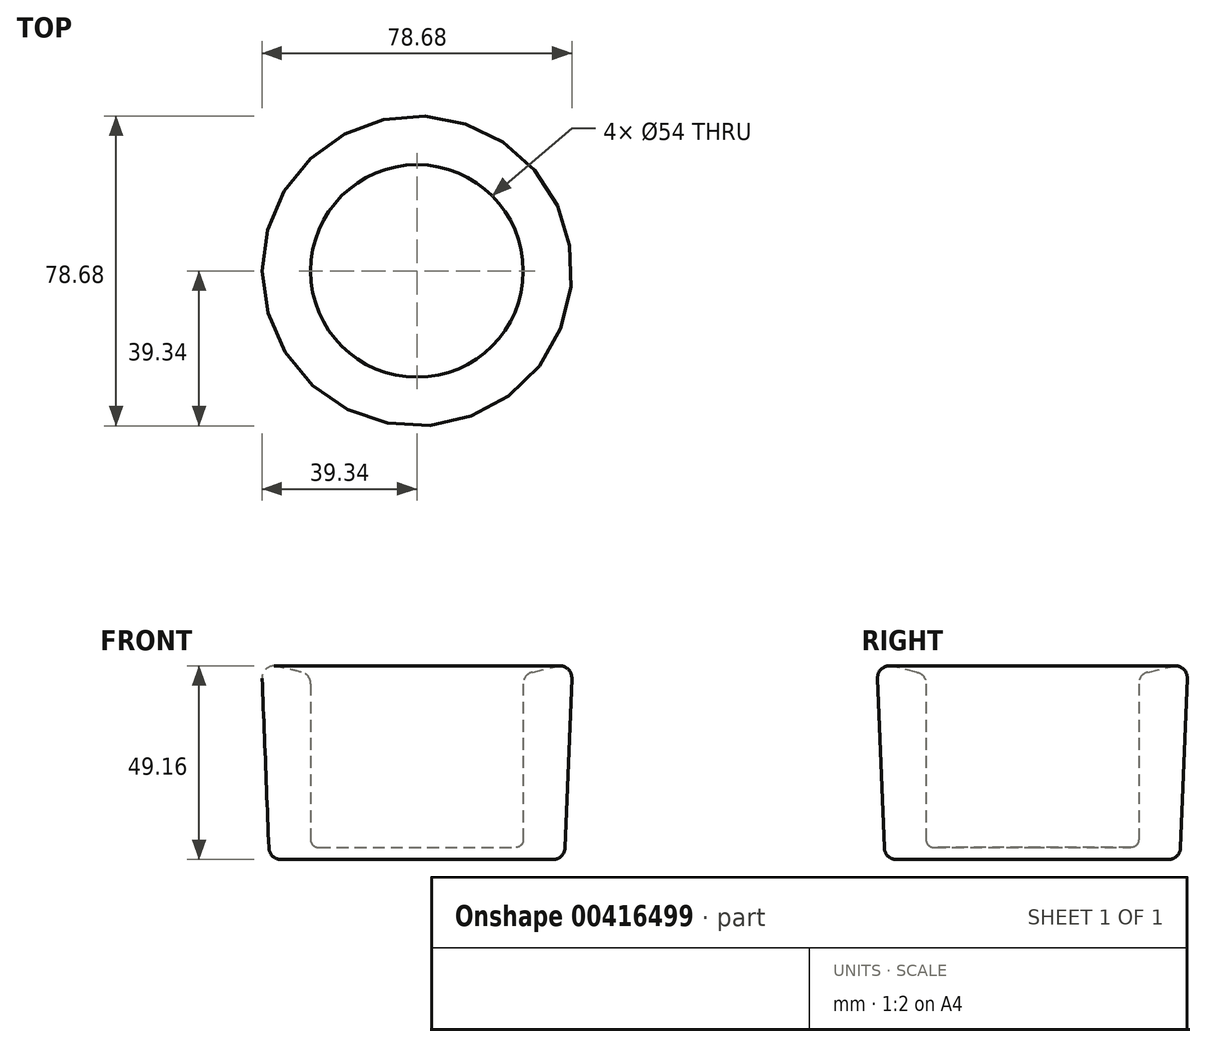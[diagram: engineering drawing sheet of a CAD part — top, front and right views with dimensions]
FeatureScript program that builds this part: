
annotation { "Feature Type Name" : "Feature", "Feature Type Description" : "" }
export const myFeature = defineFeature(function(context is Context, id is Id, definition is map)
    precondition{}
    {
        {
            var Q0;
            Q0=qCreatedBy(makeId("Right.planeOp"),FACE);
            var sketch = newSketch(context, id + "F0", { "sketchPlane" : qUnion([Q0])});
            skLineSegment(sketch, "E0", {"start": v(-39.34, 46.04) * mm, "end": v(-37.62, 2.88) * mm});
            skLineSegment(sketch, "E1", {"start": v(0, 3) * mm, "end": v(-25, 3) * mm});
            skLineSegment(sketch, "E2", {"start": v(-27, 5) * mm, "end": v(-27, 44.63) * mm});
            skLineSegment(sketch, "E3", {"start": v(-29.3, 47.55) * mm, "end": v(-35.64, 49.07) * mm});
            skLineSegment(sketch, "E4", {"start": v(-34.62, 0) * mm, "end": v(0, 0) * mm});
            skLineSegment(sketch, "E5", {"start": v(0, 0) * mm, "end": v(0, 3) * mm});
            skPoint(sketch, "E6.visualSharp", {"position": v(-39.5, 50) * mm});
            skArc(sketch, "E6.filletArc", {"start": v(-35.64, 49.07) * mm, "mid": v(-38.25, 48.48) * mm, "end": v(-39.34, 46.04) * mm});
            skPoint(sketch, "E7.visualSharp", {"position": v(-27, 47) * mm});
            skArc(sketch, "E7.filletArc", {"start": v(-27, 44.63) * mm, "mid": v(-27.64, 46.5) * mm, "end": v(-29.3, 47.55) * mm});
            skPoint(sketch, "E8.visualSharp", {"position": v(-37.5, 0) * mm});
            skArc(sketch, "E8.filletArc", {"start": v(-37.62, 2.88) * mm, "mid": v(-36.7, 0.84) * mm, "end": v(-34.62, 0) * mm});
            skPoint(sketch, "E9.visualSharp", {"position": v(-27, 3) * mm});
            skArc(sketch, "E9.filletArc", {"start": v(-27, 5) * mm, "mid": v(-26.41, 3.59) * mm, "end": v(-25, 3) * mm});
            skSolve(sketch);
        }
        {
            var Q0;
            Q0=makeQuery(id+"F0.imprint","IMPRINT",FACE,{"disambiguationData":[TD([[makeQuery(id+"F0.imprint","IMPRINT",EDGE,{"derivedFrom":sQuery(id+"F0.wireOp",EDGE,"E0")}),1.0]])]});
            var Q1;
            Q1=sQuery(id+"F0.wireOp",EDGE,"E5");
            revolve(context, id + "F1", {"entities" : qUnion([Q0]), "axis" : qUnion([Q1]), "revolveType" : RevolveType.FULL});
        }
    });
